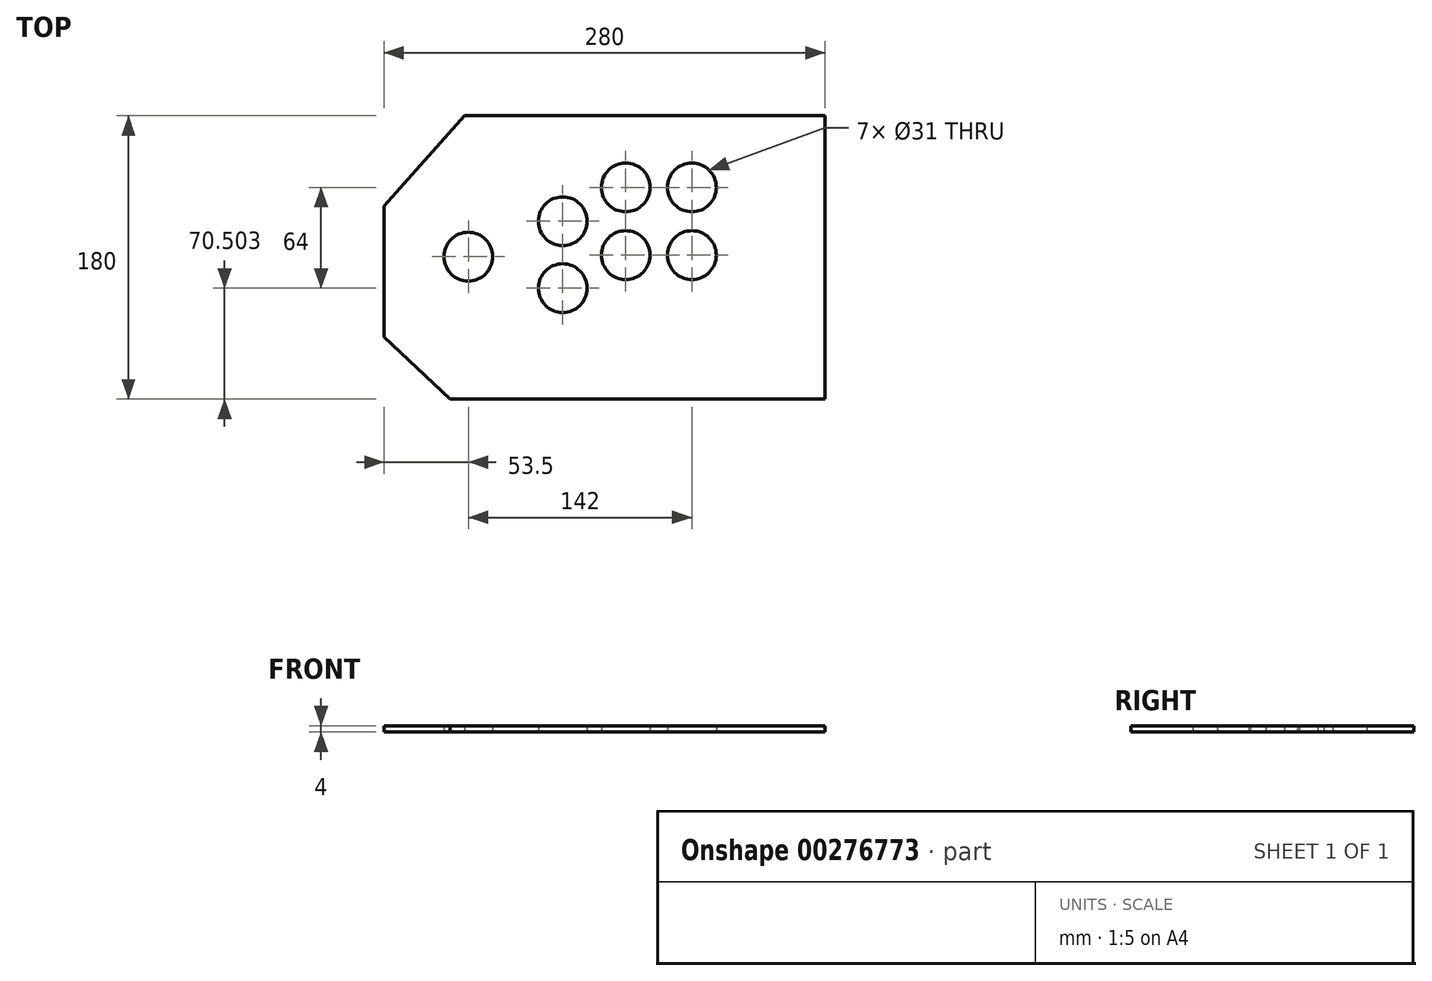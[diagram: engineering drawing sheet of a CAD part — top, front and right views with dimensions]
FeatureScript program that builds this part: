
annotation { "Feature Type Name" : "Feature", "Feature Type Description" : "" }
export const myFeature = defineFeature(function(context is Context, id is Id, definition is map)
    precondition{}
    {
        {
            var Q0;
            Q0=qCreatedBy(makeId("Top.planeOp"),FACE);
            var sketch = newSketch(context, id + "F0", { "sketchPlane" : qUnion([Q0])});
            skLineSegment(sketch, "E0.bottom", {"start": v(-135.36, 85.8) * mm, "end": v(144.64, 85.8) * mm});
            skLineSegment(sketch, "E0.top", {"start": v(-135.36, -94.2) * mm, "end": v(144.64, -94.2) * mm});
            skLineSegment(sketch, "E0.left", {"start": v(-135.36, 85.8) * mm, "end": v(-135.36, -94.2) * mm});
            skLineSegment(sketch, "E0.right", {"start": v(144.64, 85.8) * mm, "end": v(144.64, -94.2) * mm});
            skCircle(sketch, "E1", {"center": v(-81.86, -3.7) * mm, "radius": 15.5 * mm});
            skCircle(sketch, "E2", {"center": v(-21.86, 18.8) * mm, "radius": 15.5 * mm});
            skCircle(sketch, "E3", {"center": v(18.14, 40.3) * mm, "radius": 15.5 * mm});
            skCircle(sketch, "E4", {"center": v(60.14, 40.3) * mm, "radius": 15.5 * mm});
            skCircle(sketch, "E5", {"center": v(-21.86, -23.7) * mm, "radius": 15.5 * mm});
            skCircle(sketch, "E6", {"center": v(18.14, -2.7) * mm, "radius": 15.5 * mm});
            skCircle(sketch, "E7", {"center": v(60.14, -2.7) * mm, "radius": 15.5 * mm});
            skLineSegment(sketch, "E8", {"start": v(-84.31, 85.8) * mm, "end": v(-135.36, 28.43) * mm});
            skLineSegment(sketch, "E9", {"start": v(-135.36, -54.7) * mm, "end": v(-93.55, -94.2) * mm});
            skSolve(sketch);
        }
        {
            var Q0;
            {var subQ2=sQuery(id+"F0.wireOp",EDGE,"E0.right");Q0=makeQuery(id+"F0.imprint","IMPRINT",FACE,{"disambiguationData":[TD([[makeQuery(id+"F0.imprint","IMPRINT",EDGE,{"derivedFrom":subQ2}),-1.0]])]});}
            extrude(context, id + "F1", {"entities" : qUnion([Q0]), "depth" : 4 * mm});
        }
    });
